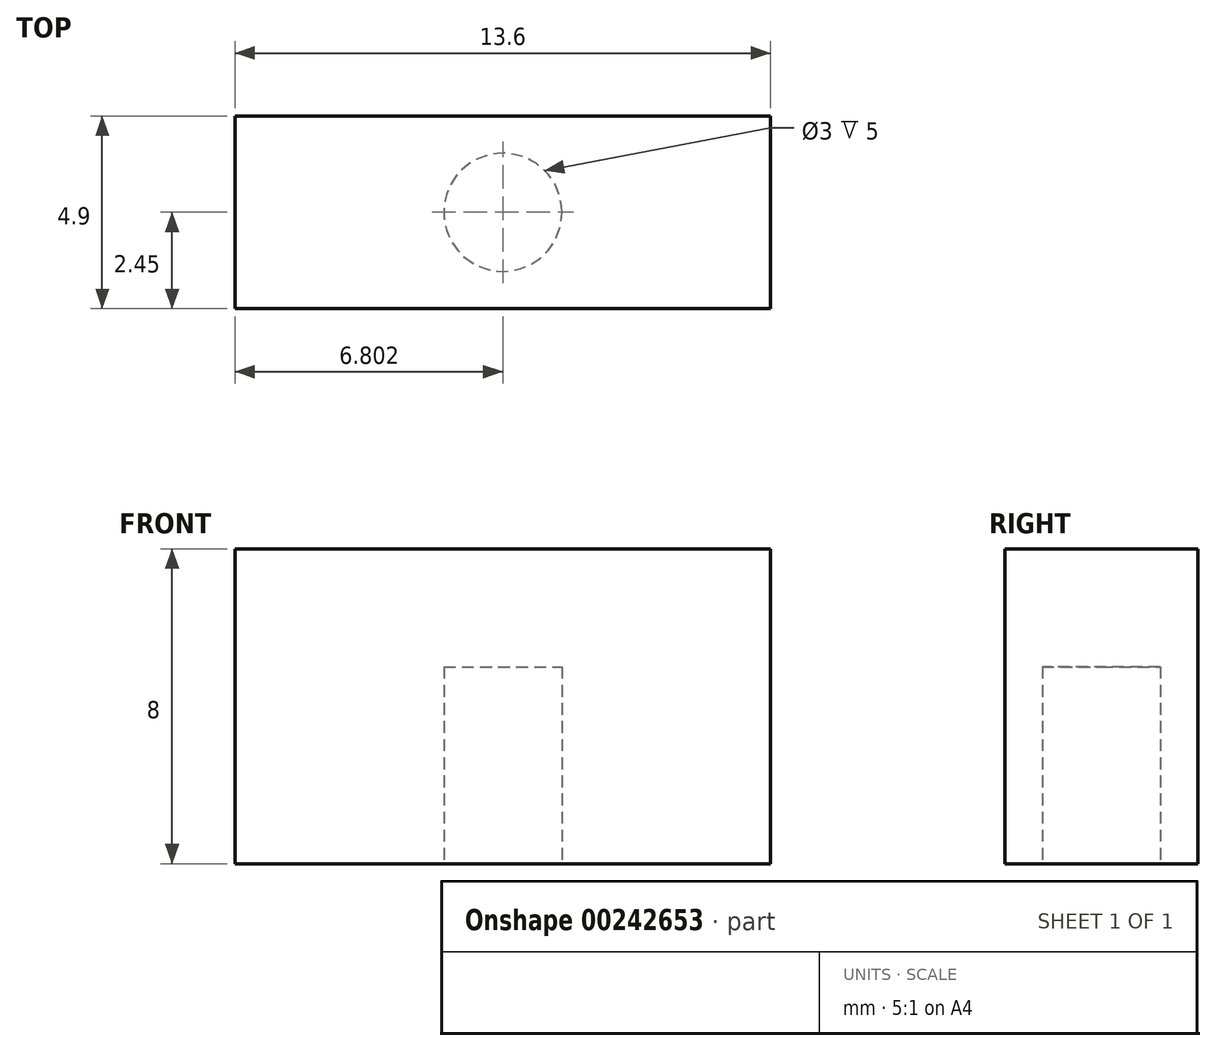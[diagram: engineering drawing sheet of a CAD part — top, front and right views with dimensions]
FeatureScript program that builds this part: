
annotation { "Feature Type Name" : "Feature", "Feature Type Description" : "" }
export const myFeature = defineFeature(function(context is Context, id is Id, definition is map)
    precondition{}
    {
        {
            var Q0;
            Q0=qCreatedBy(makeId("Top.planeOp"),FACE);
            var sketch = newSketch(context, id + "F0", { "sketchPlane" : qUnion([Q0])});
            skLineSegment(sketch, "E0.bottom", {"start": v(-55.34, 40.87) * mm, "end": v(-41.74, 40.87) * mm});
            skLineSegment(sketch, "E0.top", {"start": v(-55.34, 35.97) * mm, "end": v(-41.74, 35.97) * mm});
            skLineSegment(sketch, "E0.left", {"start": v(-55.34, 40.87) * mm, "end": v(-55.34, 35.97) * mm});
            skLineSegment(sketch, "E0.right", {"start": v(-41.74, 40.87) * mm, "end": v(-41.74, 35.97) * mm});
            skSolve(sketch);
        }
        {
            var Q0;
            Q0 = qSketchRegion(id + "F0", true);
            extrude(context, id + "F1", {"entities" : qUnion([Q0]), "depth" : 8 * mm});
        }
        {
            var Q0;
            Q0=makeQuery(id+"F1.opExtrude","CAP_FACE",FACE,{"disambiguationData":[OSD([sQuery(id+"F0.wireOp",EDGE,"E0.bottom"),sQuery(id+"F0.wireOp",EDGE,"E0.top"),sQuery(id+"F0.wireOp",EDGE,"E0.left"),sQuery(id+"F0.wireOp",EDGE,"E0.right")])],"isStart":true});
            var sketch = newSketch(context, id + "F2", { "sketchPlane" : qUnion([Q0])});
            skCircle(sketch, "E1", {"center": v(-48.54, -38.42) * mm, "radius": 1.5 * mm});
            skPoint(sketch, "E1.centerSnap0", {"position": v(-55.34, -38.42) * mm});
            skPoint(sketch, "E1.centerSnap1", {"position": v(-48.54, -35.97) * mm});
            skSolve(sketch);
        }
        {
            var Q0;
            Q0=makeQuery(id+"F2.imprint","IMPRINT",FACE,{"disambiguationData":[TD([[makeQuery(id+"F2.imprint","IMPRINT",EDGE,{"derivedFrom":sQuery(id+"F2.wireOp",EDGE,"E1")}),1.0]])]});
            extrude(context, id + "F3", {"entities" : qUnion([Q0]), "operationType" : NewBodyOperationType.REMOVE, "oppositeDirection" : true, "depth" : 5 * mm});
        }
    });
